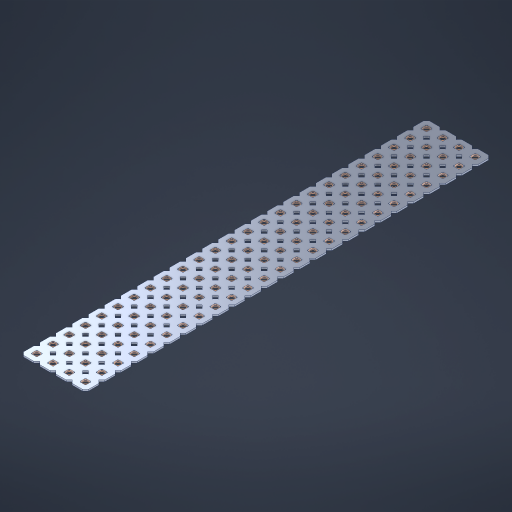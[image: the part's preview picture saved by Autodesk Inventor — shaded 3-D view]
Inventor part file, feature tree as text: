
AUTODESK INVENTOR PART (.ipt)
format: ipt  version: 2023 (Build 270158000, 158)  size: 1,420,800 bytes
history: native  units: in
note: dims shown in document units (in); Inventor stores cm internally (conversion verified against a paired STEP export)
features: other x101, extrude x99, sketch x2, pattern_linear x1
ambient origin geometry x8: Origin, YZ Plane, XZ Plane, XY Plane, X Axis, Y Axis, Z Axis, Center Point
bodies: Solid1 (feature_tree), Body (feature_tree)
feature tree (203):
  pattern_linear  "Rectangular Pattern1"  Spacing1=0.09in  [1 undecoded]
  sketch  "Sketch1"  dims[d1=0.5in]
  sketch  "Sketch2"  dims[d2=0.182in d3=0.09in d4=0.09in d5=0.09in d6=0.09in d7=0.09in d8=0.09in d9=0.09in d10=0.09in d11=0.02in d13=0.0in d14=0.172in d15=0.0625in d16=0.0in d19=0.5in d22=0.5in]
  other  "Srf1"
  other  "Srf126"
  other  "Srf127"
  other  "Srf128"
  other  "Srf129"
  other  "Srf130"
  other  "Srf131"
  other  "Srf250"
  other  "Srf251"
  other  "Srf252"
  other  "Srf253"
  other  "Srf254"
  other  "Srf255"
  other  "Srf256"
  other  "Srf257"
  other  "Srf258"
  other  "Srf259"
  other  "Srf260"
  other  "Srf261"
  other  "Srf262"
  other  "Srf263"
  other  "Srf264"
  other  "Srf265"
  other  "Srf266"
  other  "Srf267"
  other  "Srf268"
  other  "Srf269"
  other  "Srf270"
  other  "Srf271"
  other  "Srf272"
  other  "Srf273"
  other  "Srf274"
  other  "Srf275"
  other  "Srf276"
  other  "Srf277"
  other  "Srf278"
  other  "Srf279"
  other  "Srf280"
  other  "Srf281"
  other  "Srf282"
  other  "Srf283"
  other  "Srf284"
  other  "Srf285"
  other  "Srf286"
  other  "Srf287"
  other  "Srf288"
  other  "Srf289"
  other  "Srf290"
  other  "Srf291"
  other  "Srf292"
  other  "Srf293"
  other  "Srf294"
  other  "Srf295"
  other  "Srf296"
  other  "Srf297"
  other  "Srf298"
  other  "Srf299"
  other  "Srf300"
  other  "Srf301"
  other  "Srf302"
  other  "Srf303"
  other  "Srf304"
  other  "Srf305"
  other  "Srf306"
  other  "Srf307"
  other  "Srf308"
  other  "Srf309"
  other  "Srf310"
  other  "Srf311"
  other  "Srf312"
  other  "Srf313"
  other  "Srf314"
  other  "Srf315"
  other  "Srf316"
  other  "Srf317"
  other  "Srf318"
  other  "Srf319"
  other  "Srf320"
  other  "Srf321"
  other  "Srf322"
  other  "Srf323"
  other  "Srf324"
  other  "Srf325"
  other  "Srf326"
  other  "Srf327"
  other  "Srf328"
  other  "Srf329"
  other  "Srf330"
  other  "Srf331"
  other  "Srf332"
  other  "Srf333"
  other  "Srf334"
  other  "Srf335"
  other  "Srf336"
  other  "Srf337"
  other  "Srf338"
  other  "Srf339"
  other  "Srf340"
  other  "Srf341"
  other  "Srf342"
  other  "Circle"
  extrude  "ExtrusionSrf126"  Depth=0.09in
  extrude  "ExtrusionSrf127"  Depth=0.09in
  extrude  "ExtrusionSrf128"  Depth=0.09in
  extrude  "ExtrusionSrf129"  Depth=0.09in
  extrude  "ExtrusionSrf130"  Depth=0.09in
  extrude  "ExtrusionSrf131"  Depth=0.09in
  extrude  "ExtrusionSrf250"  Depth=0.09in
  extrude  "ExtrusionSrf251"  Depth=0.02in
  extrude  "ExtrusionSrf252"  TaperAngle=0.0deg  [1 undecoded]
  extrude  "ExtrusionSrf253"  Depth=0.5in
  extrude  "ExtrusionSrf254"  Depth=0.5in TaperAngle=0.0deg
  extrude  "ExtrusionSrf255"  Depth=0.5in
  extrude  "ExtrusionSrf256"  Depth=0.5in
  extrude  "ExtrusionSrf257"  [1 undecoded]
  extrude  "ExtrusionSrf258"  [1 undecoded]
  extrude  "ExtrusionSrf259"  [1 undecoded]
  extrude  "ExtrusionSrf260"  [1 undecoded]
  extrude  "ExtrusionSrf261"  [1 undecoded]
  extrude  "ExtrusionSrf262"  [1 undecoded]
  extrude  "ExtrusionSrf263"  [1 undecoded]
  extrude  "ExtrusionSrf264"  [1 undecoded]
  extrude  "ExtrusionSrf265"  [1 undecoded]
  extrude  "ExtrusionSrf266"  [1 undecoded]
  extrude  "ExtrusionSrf267"  [1 undecoded]
  extrude  "ExtrusionSrf268"  [1 undecoded]
  extrude  "ExtrusionSrf269"  [1 undecoded]
  extrude  "ExtrusionSrf270"  [1 undecoded]
  extrude  "ExtrusionSrf271"  [1 undecoded]
  extrude  "ExtrusionSrf272"  [1 undecoded]
  extrude  "ExtrusionSrf273"  [1 undecoded]
  extrude  "ExtrusionSrf274"  [1 undecoded]
  extrude  "ExtrusionSrf275"  [1 undecoded]
  extrude  "ExtrusionSrf276"  [1 undecoded]
  extrude  "ExtrusionSrf277"  [1 undecoded]
  extrude  "ExtrusionSrf278"  [1 undecoded]
  extrude  "ExtrusionSrf279"  [1 undecoded]
  extrude  "ExtrusionSrf280"  [1 undecoded]
  extrude  "ExtrusionSrf281"  [1 undecoded]
  extrude  "ExtrusionSrf282"  [1 undecoded]
  extrude  "ExtrusionSrf283"  [1 undecoded]
  extrude  "ExtrusionSrf284"  [1 undecoded]
  extrude  "ExtrusionSrf285"  [1 undecoded]
  extrude  "ExtrusionSrf286"  [1 undecoded]
  extrude  "ExtrusionSrf287"  [1 undecoded]
  extrude  "ExtrusionSrf288"  [1 undecoded]
  extrude  "ExtrusionSrf289"  [1 undecoded]
  extrude  "ExtrusionSrf290"  [1 undecoded]
  extrude  "ExtrusionSrf291"  [1 undecoded]
  extrude  "ExtrusionSrf292"  [1 undecoded]
  extrude  "ExtrusionSrf293"  [1 undecoded]
  extrude  "ExtrusionSrf294"  [1 undecoded]
  extrude  "ExtrusionSrf295"  [1 undecoded]
  extrude  "ExtrusionSrf296"  [1 undecoded]
  extrude  "ExtrusionSrf297"  [1 undecoded]
  extrude  "ExtrusionSrf298"  [1 undecoded]
  extrude  "ExtrusionSrf299"  [1 undecoded]
  extrude  "ExtrusionSrf300"  [1 undecoded]
  extrude  "ExtrusionSrf301"  [1 undecoded]
  extrude  "ExtrusionSrf302"  [1 undecoded]
  extrude  "ExtrusionSrf303"  [1 undecoded]
  extrude  "ExtrusionSrf304"  [1 undecoded]
  extrude  "ExtrusionSrf305"  [1 undecoded]
  extrude  "ExtrusionSrf306"  [1 undecoded]
  extrude  "ExtrusionSrf307"  [1 undecoded]
  extrude  "ExtrusionSrf308"  [1 undecoded]
  extrude  "ExtrusionSrf309"  [1 undecoded]
  extrude  "ExtrusionSrf310"  [1 undecoded]
  extrude  "ExtrusionSrf311"  [1 undecoded]
  extrude  "ExtrusionSrf312"  [1 undecoded]
  extrude  "ExtrusionSrf313"  [1 undecoded]
  extrude  "ExtrusionSrf314"  [1 undecoded]
  extrude  "ExtrusionSrf315"  [1 undecoded]
  extrude  "ExtrusionSrf316"  [1 undecoded]
  extrude  "ExtrusionSrf317"  [1 undecoded]
  extrude  "ExtrusionSrf318"  [1 undecoded]
  extrude  "ExtrusionSrf319"  [1 undecoded]
  extrude  "ExtrusionSrf320"  [1 undecoded]
  extrude  "ExtrusionSrf321"  [1 undecoded]
  extrude  "ExtrusionSrf322"  [1 undecoded]
  extrude  "ExtrusionSrf323"  [1 undecoded]
  extrude  "ExtrusionSrf324"  [1 undecoded]
  extrude  "ExtrusionSrf325"  [1 undecoded]
  extrude  "ExtrusionSrf326"  [1 undecoded]
  extrude  "ExtrusionSrf327"  [1 undecoded]
  extrude  "ExtrusionSrf328"  [1 undecoded]
  extrude  "ExtrusionSrf329"  [1 undecoded]
  extrude  "ExtrusionSrf330"  [1 undecoded]
  extrude  "ExtrusionSrf331"  [1 undecoded]
  extrude  "ExtrusionSrf332"  [1 undecoded]
  extrude  "ExtrusionSrf333"  [1 undecoded]
  extrude  "ExtrusionSrf334"  [1 undecoded]
  extrude  "ExtrusionSrf335"  [1 undecoded]
  extrude  "ExtrusionSrf336"  [1 undecoded]
  extrude  "ExtrusionSrf337"  [1 undecoded]
  extrude  "ExtrusionSrf338"  [1 undecoded]
  extrude  "ExtrusionSrf339"  [1 undecoded]
  extrude  "ExtrusionSrf340"  [1 undecoded]
  extrude  "ExtrusionSrf341"  [1 undecoded]
  extrude  "ExtrusionSrf342"  [1 undecoded]
note: 88 required parameter values undecoded (feature->parameter linkage not recoverable at this tier; creation-order binding heuristic only, values carry confidence <= 0.55)
